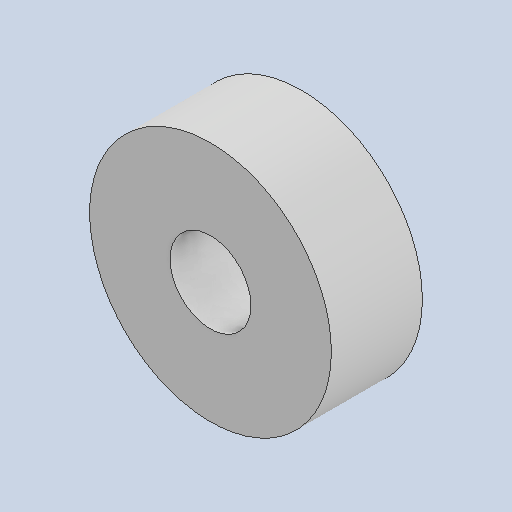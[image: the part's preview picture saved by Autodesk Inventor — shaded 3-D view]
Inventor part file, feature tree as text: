
AUTODESK INVENTOR PART (.ipt)
format: ipt  version: 2023 (Build 270158000, 158)  size: 136,192 bytes
history: native  units: in
note: dims shown in document units (in); Inventor stores cm internally (conversion verified against a paired STEP export)
features: extrude x1, sketch x1
ambient origin geometry x8: Origin, YZ Plane, XZ Plane, XY Plane, X Axis, Y Axis, Z Axis, Center Point
bodies: Solid1 (feature_tree)
feature tree (2):
  extrude  "Extrusion1"  Depth=0.2812in
  sketch  "Sketch1"  dims[d0=0.25in d1=0.747in d2=0.2812in d3=0.0in]
